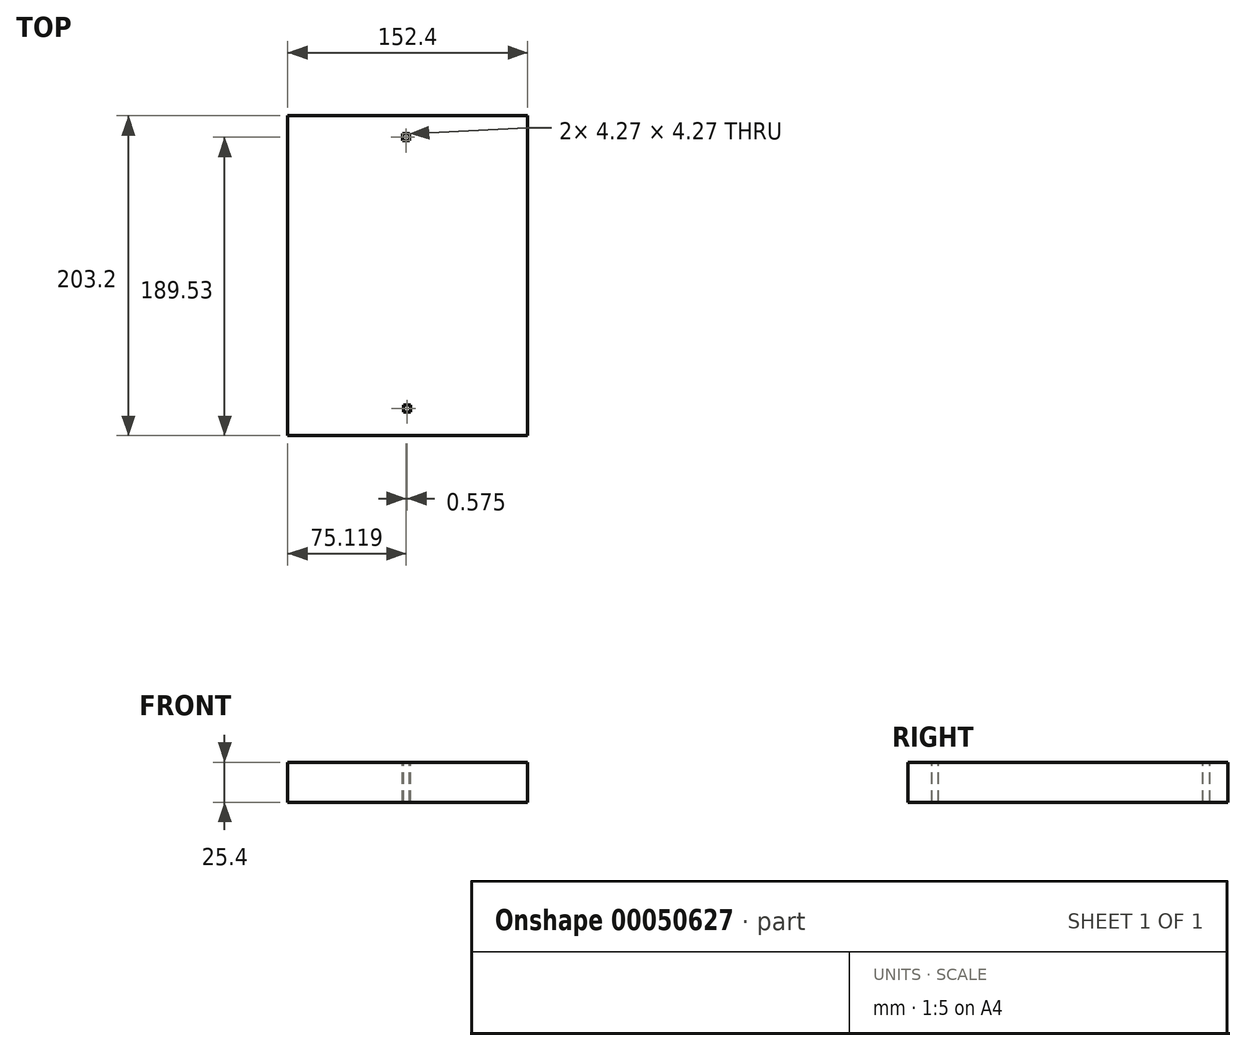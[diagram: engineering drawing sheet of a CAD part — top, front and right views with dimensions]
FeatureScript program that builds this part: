
annotation { "Feature Type Name" : "Feature", "Feature Type Description" : "" }
export const myFeature = defineFeature(function(context is Context, id is Id, definition is map)
    precondition{}
    {
        {
            var Q0;
            Q0=qCreatedBy(makeId("Top.planeOp"),FACE);
            var sketch = newSketch(context, id + "F0", { "sketchPlane" : qUnion([Q0])});
            skLineSegment(sketch, "E0.bottom", {"start": v(-107.81, 99.14) * mm, "end": v(44.59, 99.14) * mm});
            skLineSegment(sketch, "E0.top", {"start": v(-107.81, -104.06) * mm, "end": v(44.59, -104.06) * mm});
            skLineSegment(sketch, "E0.left", {"start": v(-107.81, 99.14) * mm, "end": v(-107.81, -104.06) * mm});
            skLineSegment(sketch, "E0.right", {"start": v(44.59, 99.14) * mm, "end": v(44.59, -104.06) * mm});
            skSolve(sketch);
        }
        {
            var Q0;
            Q0=makeQuery(id+"F0.imprint","IMPRINT",FACE,{"disambiguationData":[TD([[makeQuery(id+"F0.imprint","IMPRINT",EDGE,{"derivedFrom":sQuery(id+"F0.wireOp",EDGE,"E0.bottom")}),-1.0]])]});
            var sketch = newSketch(context, id + "F1", { "sketchPlane" : qUnion([Q0])});
            skSolve(sketch);
        }
        {
            var Q0;
            Q0 = qSketchRegion(id + "F1", true);
            var Q1;
            Q1=makeQuery(id+"F0.imprint","IMPRINT",FACE,{"disambiguationData":[TD([[makeQuery(id+"F0.imprint","IMPRINT",EDGE,{"derivedFrom":sQuery(id+"F0.wireOp",EDGE,"E0.bottom")}),-1.0]])]});
            extrude(context, id + "F2", {"entities" : qUnion([Q0, Q1]), "depth" : 25.4 * mm});
        }
        {
            var Q0;
            Q0=makeQuery(id+"F2.opExtrude","CAP_FACE",FACE,{"disambiguationData":[OSD([sQuery(id+"F0.wireOp",EDGE,"E0.bottom"),sQuery(id+"F0.wireOp",EDGE,"E0.top"),sQuery(id+"F0.wireOp",EDGE,"E0.left"),sQuery(id+"F0.wireOp",EDGE,"E0.right")])],"isStart":false});
            var sketch = newSketch(context, id + "F3", { "sketchPlane" : qUnion([Q0])});
            skLineSegment(sketch, "E1.bottom", {"start": v(-34.82, 87.6) * mm, "end": v(-30.56, 87.6) * mm});
            skLineSegment(sketch, "E1.top", {"start": v(-34.82, 83.34) * mm, "end": v(-30.56, 83.34) * mm});
            skLineSegment(sketch, "E1.left", {"start": v(-34.82, 87.6) * mm, "end": v(-34.82, 83.34) * mm});
            skLineSegment(sketch, "E1.right", {"start": v(-30.56, 87.6) * mm, "end": v(-30.56, 83.34) * mm});
            skLineSegment(sketch, "E2.bottom", {"start": v(-30.66, -89.11) * mm, "end": v(-26.4, -89.11) * mm});
            skLineSegment(sketch, "E2.top", {"start": v(-30.66, -84.84) * mm, "end": v(-26.4, -84.84) * mm});
            skLineSegment(sketch, "E2.left", {"start": v(-30.66, -89.11) * mm, "end": v(-30.66, -84.84) * mm});
            skLineSegment(sketch, "E2.right", {"start": v(-26.4, -89.11) * mm, "end": v(-26.4, -84.84) * mm});
            skSolve(sketch);
        }
        {
            var Q0;
            Q0 = qSketchRegion(id + "FVjvwONjhBQtjsK_1", true);
            var Q1;
            Q1=makeQuery(id+"F3.imprint","IMPRINT",FACE,{"disambiguationData":[TD([[makeQuery(id+"F3.imprint","IMPRINT",EDGE,{"derivedFrom":sQuery(id+"F3.wireOp",EDGE,"E1.bottom")}),-1.0]])]});
            extrude(context, id + "F4", {"entities" : qUnion([Q0, Q1]), "operationType" : NewBodyOperationType.REMOVE, "endBound" : BoundingType.THROUGH_ALL, "oppositeDirection" : true, "depth" : 25.4 * mm});
        }
        {
            var Q0;
            Q0=makeQuery(id+"F2.opExtrude","CAP_FACE",FACE,{"disambiguationData":[OSD([sQuery(id+"F0.wireOp",EDGE,"E0.bottom"),sQuery(id+"F0.wireOp",EDGE,"E0.top"),sQuery(id+"F0.wireOp",EDGE,"E0.left"),sQuery(id+"F0.wireOp",EDGE,"E0.right")])],"isStart":false});
            var sketch = newSketch(context, id + "F5", { "sketchPlane" : qUnion([Q0])});
            skLineSegment(sketch, "E3.bottom", {"start": v(-34.25, -89.04) * mm, "end": v(-29.98, -89.04) * mm});
            skLineSegment(sketch, "E3.top", {"start": v(-34.25, -84.77) * mm, "end": v(-29.98, -84.77) * mm});
            skLineSegment(sketch, "E3.left", {"start": v(-34.25, -89.04) * mm, "end": v(-34.25, -84.77) * mm});
            skLineSegment(sketch, "E3.right", {"start": v(-29.98, -89.04) * mm, "end": v(-29.98, -84.77) * mm});
            skSolve(sketch);
        }
        {
            var Q0;
            Q0=makeQuery(id+"F5.imprint","IMPRINT",FACE,{"disambiguationData":[TD([[makeQuery(id+"F5.imprint","IMPRINT",EDGE,{"derivedFrom":sQuery(id+"F5.wireOp",EDGE,"E3.bottom")}),1.0]])]});
            extrude(context, id + "F6", {"entities" : qUnion([Q0]), "operationType" : NewBodyOperationType.REMOVE, "endBound" : BoundingType.THROUGH_ALL, "oppositeDirection" : true, "depth" : 25.4 * mm});
        }
    });
